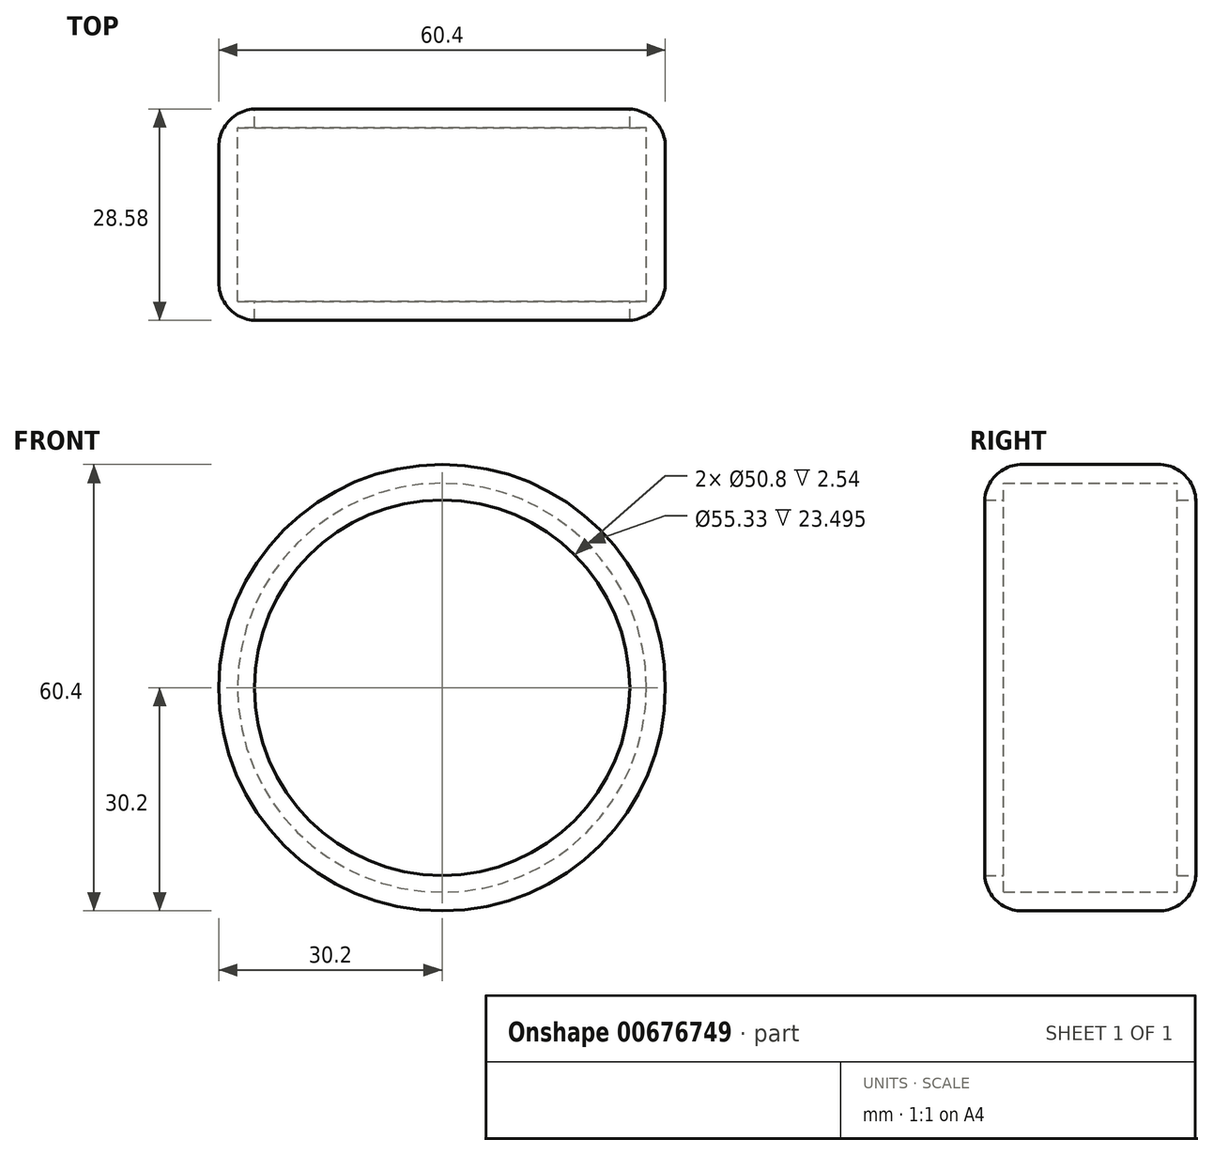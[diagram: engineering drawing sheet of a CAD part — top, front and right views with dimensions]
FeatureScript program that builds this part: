
annotation { "Feature Type Name" : "Feature", "Feature Type Description" : "" }
export const myFeature = defineFeature(function(context is Context, id is Id, definition is map)
    precondition{}
    {
        {
            var Q0;
            Q0=qCreatedBy(makeId("Front.planeOp"),FACE);
            var sketch = newSketch(context, id + "F0", { "sketchPlane" : qUnion([Q0])});
            skCircle(sketch, "E0", {"center": v(0, 0) * mm, "radius": 23.02 * mm});
            skCircle(sketch, "E1", {"center": v(0, 0) * mm, "radius": 25.4 * mm});
            skCircle(sketch, "E2", {"center": v(0, 0) * mm, "radius": 30.2 * mm});
            skSolve(sketch);
        }
        {
            var Q0;
            Q0=qCreatedBy(makeId("Top.planeOp"),FACE);
            cPlane(context, id + "F1", {"entities" : qUnion([Q0]), "cplaneType" : CPlaneType.OFFSET, "offset" : 23.37 * mm, "width" : 152.4 * mm, "height" : 152.4 * mm});
        }
        {
            var Q0;
            Q0=makeQuery(id+"F0.imprint","IMPRINT",FACE,{"disambiguationData":[TD([[makeQuery(id+"F0.imprint","IMPRINT",EDGE,{"derivedFrom":sQuery(id+"F0.wireOp",EDGE,"E1")}),-1.0]])]});
            extrude(context, id + "F2", {"entities" : qUnion([Q0]), "depth" : 28.57 * mm, "offsetDistance" : 25.4 * mm});
        }
        {
            var Q0;
            Q0=makeQuery(id+"F2.opExtrude","SWEPT_FACE",FACE,{"disambiguationData":[OSD([sQuery(id+"F0.wireOp",EDGE,"E1")])]});
            shell(context, id + "F3", {"entities" : qUnion([Q0]), "thickness" : 2.54 * mm});
        }
        {
            var Q0;
            Q0=makeQuery(id+"F2.opExtrude","CAP_EDGE",EDGE,{"disambiguationData":[OSD([sQuery(id+"F0.wireOp",EDGE,"E2")])],"isStart":true});
            var Q1;
            Q1=makeQuery(id+"F2.opExtrude","CAP_EDGE",EDGE,{"disambiguationData":[OSD([sQuery(id+"F0.wireOp",EDGE,"E2")])],"isStart":false});
            fillet(context, id + "F4", {"entities" : qUnion([Q0, Q1]), "radius" : 5.08 * mm, "tangentPropagation" : true, "allowEdgeOverflow" : false});
        }
    });
